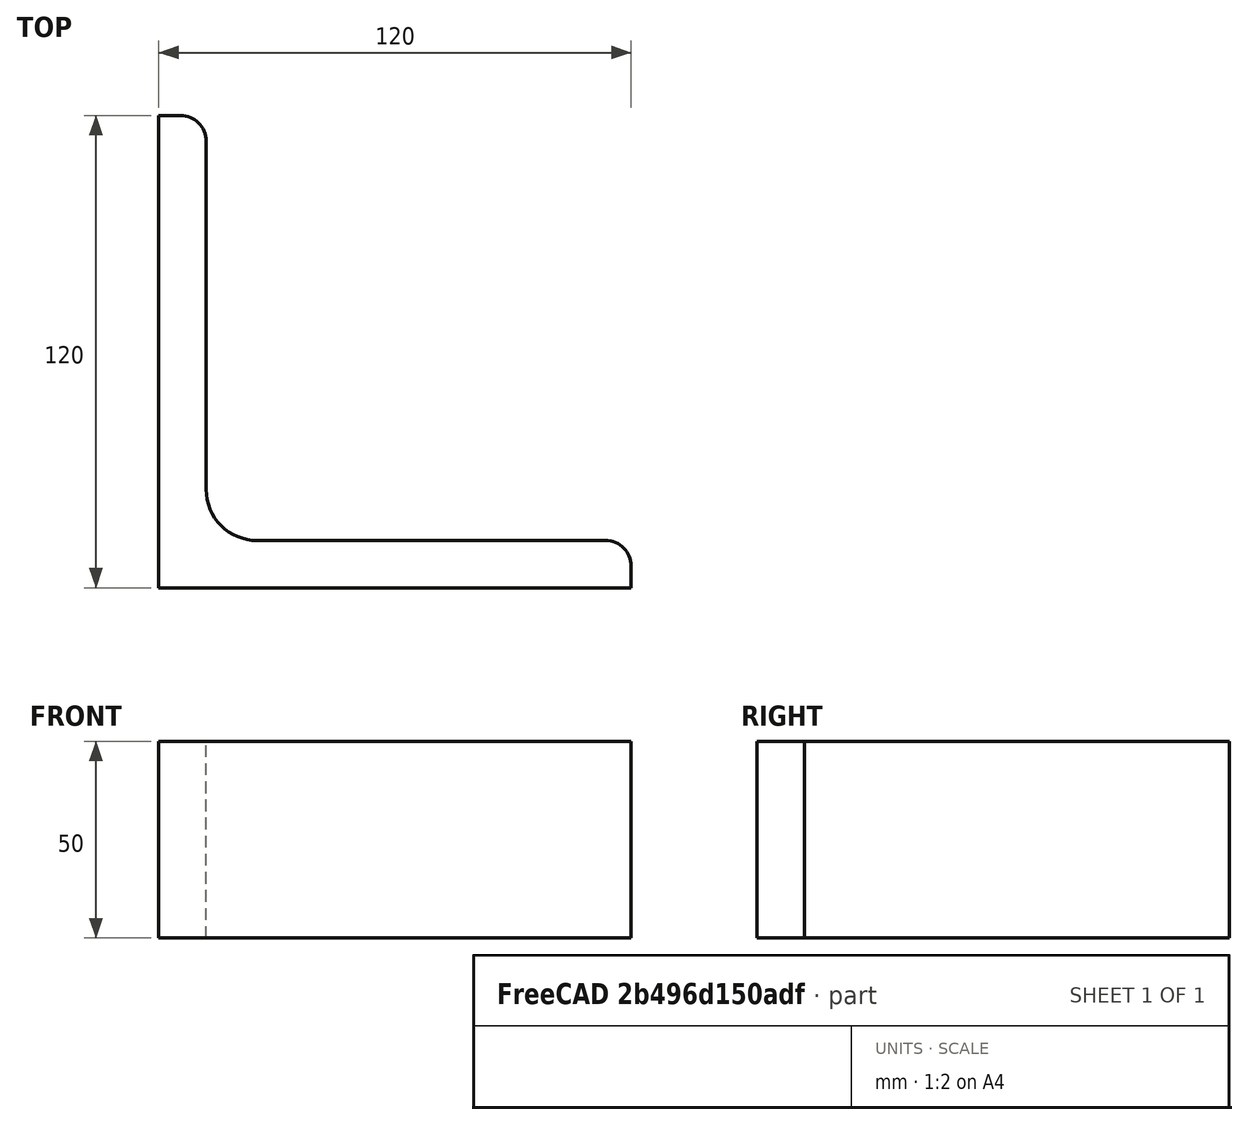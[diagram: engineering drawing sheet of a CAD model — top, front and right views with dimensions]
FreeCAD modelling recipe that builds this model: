
FCSTD DOCUMENT  (FreeCAD 0.15R4671 (Git))
Label: Angle Bar L120x120x12 EN10056 S235JR
License: All rights reserved
LicenseURL: http://en.wikipedia.org/wiki/All_rights_reserved
objects: Sketcher::SketchObject×1, Part::Extrusion×1
note: 2 computed .brp shape members not serialized (recipe doc carries the construction recipe); baked Part::Feature solids carry a one-line shape summary decoded from their .brp

FEATURE [Sketcher::SketchObject] Sketch
  sketch-geometry (9):
    g0: LineSegment StartX=0 StartY=0 StartZ=0 EndX=120 EndY=0 EndZ=0
    g1: LineSegment StartX=120 StartY=0 StartZ=0 EndX=120 EndY=5.5 EndZ=0
    g2: LineSegment StartX=113.5 StartY=12 StartZ=0 EndX=25 EndY=12 EndZ=0
    g3: LineSegment StartX=0 StartY=0 StartZ=0 EndX=0 EndY=120 EndZ=0
    g4: LineSegment StartX=0 StartY=120 StartZ=0 EndX=5.5 EndY=120 EndZ=0
    g5: LineSegment StartX=12 StartY=113.5 StartZ=0 EndX=12 EndY=25 EndZ=0
    g6: ArcOfCircle CenterX=25 CenterY=25 CenterZ=0 NormalX=0 NormalY=0 NormalZ=1 Radius=13 StartAngle=3.14159 EndAngle=4.71239
    g7: ArcOfCircle CenterX=5.5 CenterY=113.5 CenterZ=0 NormalX=0 NormalY=0 NormalZ=1 Radius=6.5 StartAngle=0 EndAngle=1.5708
    g8: ArcOfCircle CenterX=113.5 CenterY=5.5 CenterZ=0 NormalX=0 NormalY=0 NormalZ=1 Radius=6.5 StartAngle=0 EndAngle=1.5708
  constraints (23):
    c: Coincident(g0,g-1)
    c: Horizontal(g0)
    c: Coincident(g1,g0)
    c: Vertical(g1)
    c: Horizontal(g2)
    c: Coincident(g3,g-1)
    c: Vertical(g3)
    c: Coincident(g4,g3)
    c: Horizontal(g4)
    c: Vertical(g5)
    c: Tangent(g5,g6) = -1.5708
    c: Tangent(g2,g6) = 1.5708
    c: Tangent(g4,g7) = 1.5708
    c: Tangent(g5,g7) = 1.5708
    c: Tangent(g2,g8) = -1.5708
    c: Tangent(g1,g8) = -1.5708
    c: DistanceX(g0) = 120
    c: DistanceY(g3) = 120
    c: DistanceY(g0,g2) = 12
    c: DistanceX(g3,g5) = 12
    c: Radius(g6) = 13
    c: Radius(g8) = 6.5
    c: Radius(g7) = 6.5
FEATURE [Part::Extrusion] Extrude  label="Angle Bar L120x120x12 EN10056 S235JR"
  Base = -> Sketch
  Dir = (0,0,50)
  Solid = true
